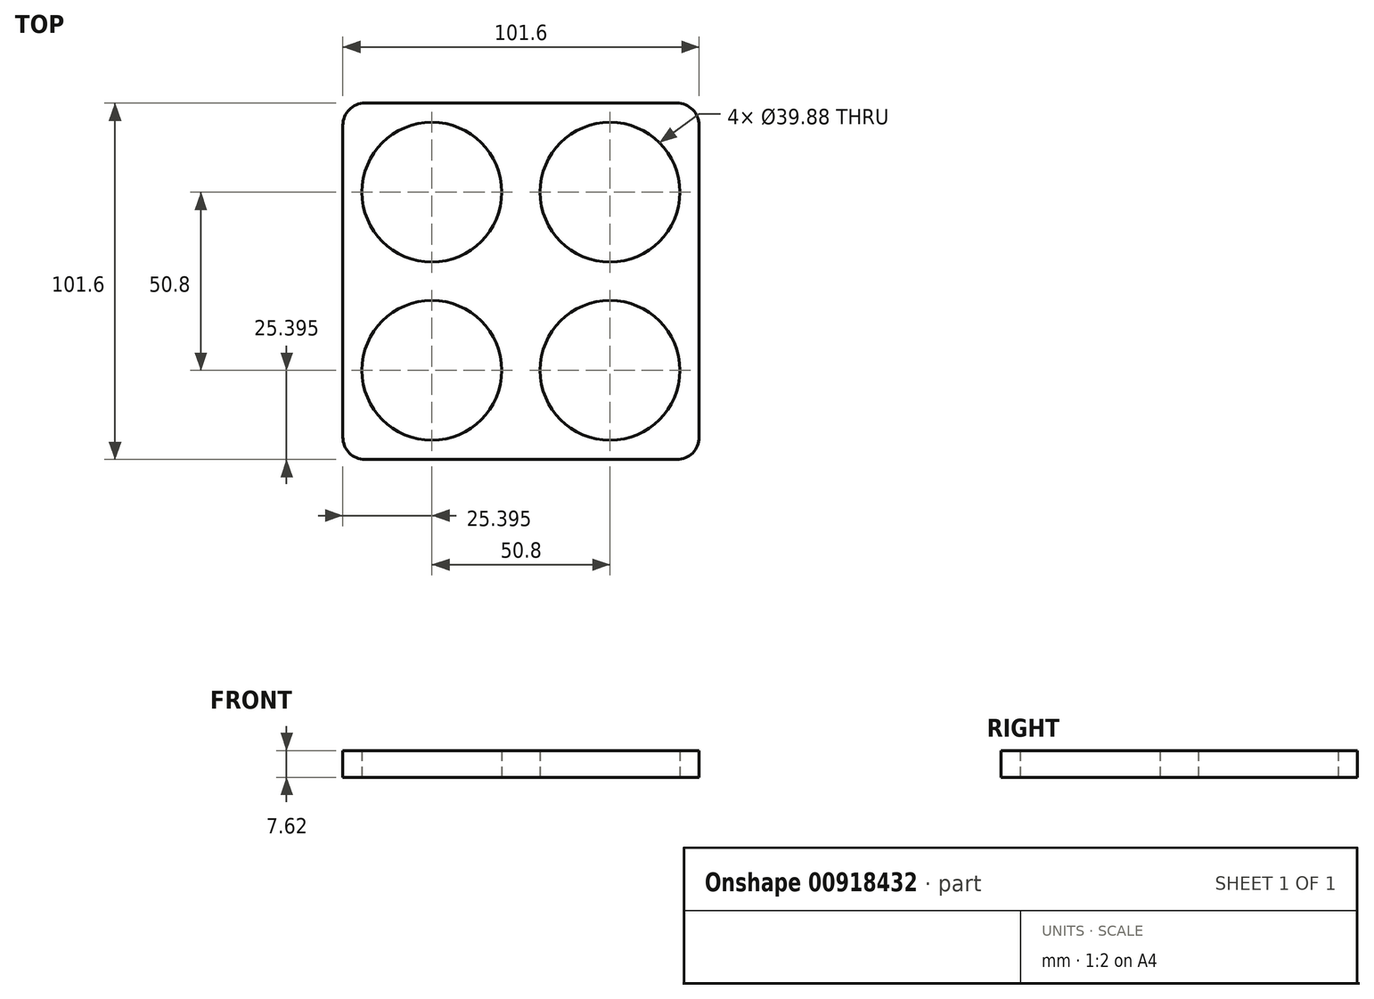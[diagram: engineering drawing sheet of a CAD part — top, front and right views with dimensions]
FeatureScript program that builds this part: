
annotation { "Feature Type Name" : "Feature", "Feature Type Description" : "" }
export const myFeature = defineFeature(function(context is Context, id is Id, definition is map)
    precondition{}
    {
        {
            var Q0;
            Q0=qCreatedBy(makeId("Top.planeOp"),FACE);
            var sketch = newSketch(context, id + "F0", { "sketchPlane" : qUnion([Q0])});
            skLineSegment(sketch, "E0.bottom", {"start": v(-37.6, -47.61) * mm, "end": v(51.3, -47.61) * mm});
            skLineSegment(sketch, "E0.top", {"start": v(-37.6, 53.99) * mm, "end": v(51.3, 53.99) * mm});
            skLineSegment(sketch, "E0.left", {"start": v(-43.94, -41.26) * mm, "end": v(-43.94, 47.64) * mm});
            skLineSegment(sketch, "E0.right", {"start": v(57.66, -41.26) * mm, "end": v(57.66, 47.64) * mm});
            skPoint(sketch, "E1", {"position": v(6.86, 3.19) * mm});
            skCircle(sketch, "E2", {"center": v(-18.54, 28.59) * mm, "radius": 19.94 * mm});
            skCircle(sketch, "E3", {"center": v(32.26, 28.59) * mm, "radius": 19.94 * mm});
            skCircle(sketch, "E4", {"center": v(-18.54, -22.21) * mm, "radius": 19.94 * mm});
            skCircle(sketch, "E5", {"center": v(32.26, -22.21) * mm, "radius": 19.94 * mm});
            skPoint(sketch, "E6.visualSharp", {"position": v(-43.94, 53.99) * mm});
            skArc(sketch, "E6.filletArc", {"start": v(-37.6, 53.99) * mm, "mid": v(-42.08, 52.13) * mm, "end": v(-43.94, 47.64) * mm});
            skPoint(sketch, "E7.visualSharp", {"position": v(-43.94, -47.61) * mm});
            skArc(sketch, "E7.filletArc", {"start": v(-43.94, -41.26) * mm, "mid": v(-42.08, -45.75) * mm, "end": v(-37.6, -47.61) * mm});
            skPoint(sketch, "E8.visualSharp", {"position": v(57.66, -47.61) * mm});
            skArc(sketch, "E8.filletArc", {"start": v(51.3, -47.61) * mm, "mid": v(55.8, -45.75) * mm, "end": v(57.66, -41.26) * mm});
            skPoint(sketch, "E9.visualSharp", {"position": v(57.66, 53.99) * mm});
            skArc(sketch, "E9.filletArc", {"start": v(57.66, 47.64) * mm, "mid": v(55.8, 52.13) * mm, "end": v(51.3, 53.99) * mm});
            skSolve(sketch);
        }
        {
            var Q0;
            Q0=makeQuery(id+"F0.imprint","IMPRINT",FACE,{"disambiguationData":[TD([[makeQuery(id+"F0.imprint","IMPRINT",EDGE,{"derivedFrom":sQuery(id+"F0.wireOp",EDGE,"E0.bottom")}),1.0]])]});
            var Q1;
            Q1=makeQuery(id+"F0.imprint","IMPRINT",FACE,{"disambiguationData":[TD([[makeQuery(id+"F0.imprint","IMPRINT",EDGE,{"derivedFrom":sQuery(id+"F0.wireOp",EDGE,"x6Vx0Ko4-JDVN-jSV2-B9Qe-zJZrQC9SNdCG")}),1.0]])]});
            extrude(context, id + "F1", {"entities" : qUnion([Q0, Q1]), "depth" : 7.62 * mm, "offsetDistance" : 25.4 * mm});
        }
    });
